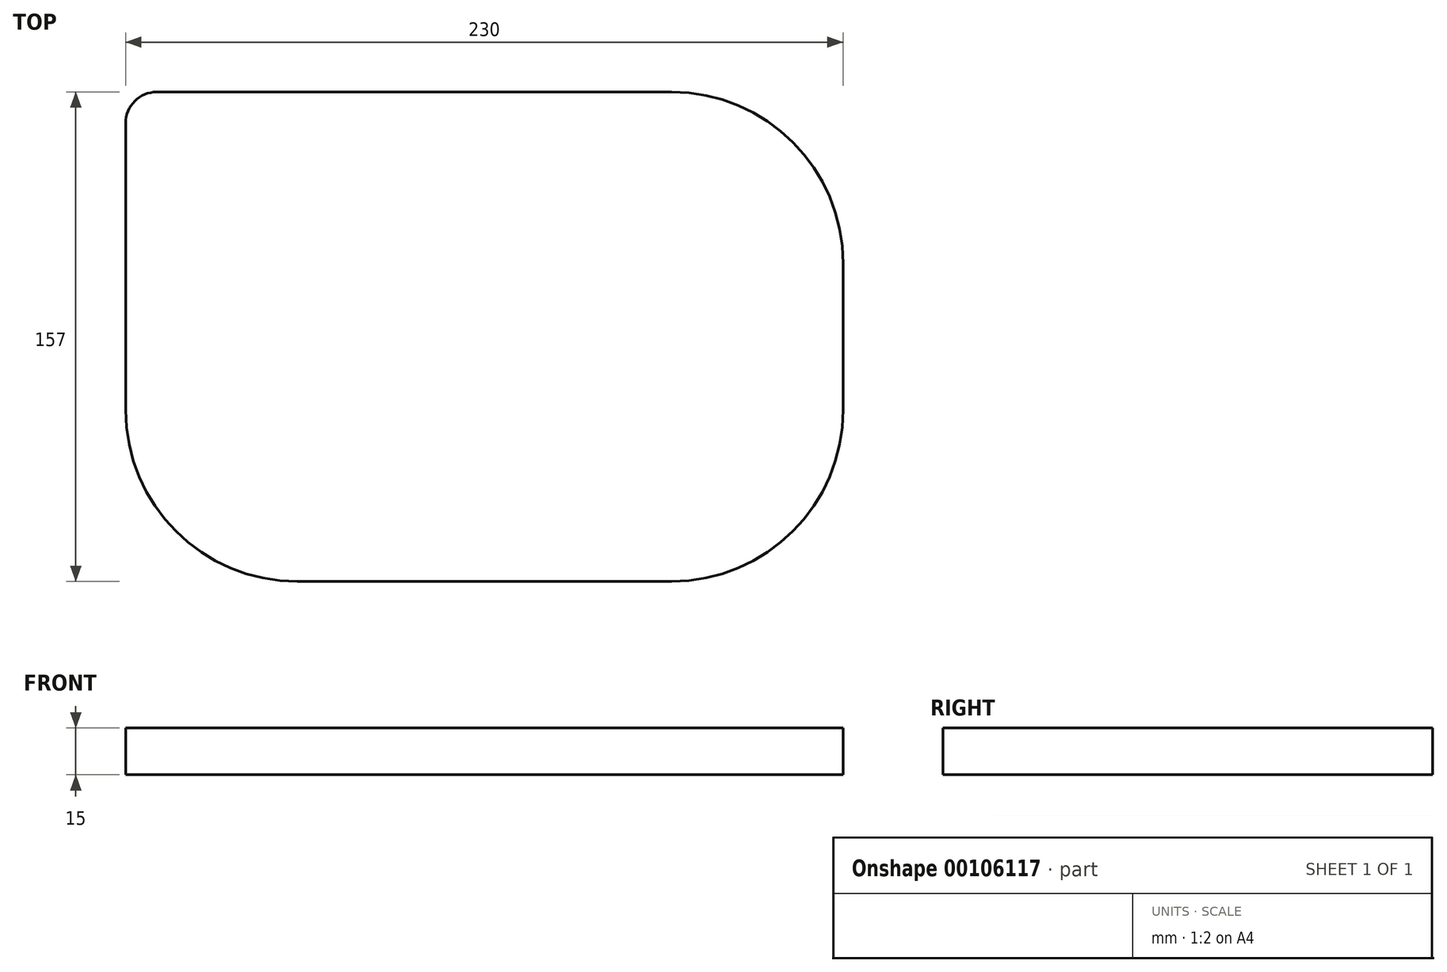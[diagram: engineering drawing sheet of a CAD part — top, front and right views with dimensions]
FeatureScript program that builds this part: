
annotation { "Feature Type Name" : "Feature", "Feature Type Description" : "" }
export const myFeature = defineFeature(function(context is Context, id is Id, definition is map)
    precondition{}
    {
        {
            var Q0;
            Q0=qCreatedBy(makeId("Top.planeOp"),FACE);
            var sketch = newSketch(context, id + "F0", { "sketchPlane" : qUnion([Q0])});
            skLineSegment(sketch, "E0.bottom", {"start": v(60, -78.5) * mm, "end": v(-60, -78.5) * mm});
            skLineSegment(sketch, "E0.top", {"start": v(60, 78.5) * mm, "end": v(-105, 78.5) * mm});
            skLineSegment(sketch, "E0.left", {"start": v(115, -23.5) * mm, "end": v(115, 23.5) * mm});
            skLineSegment(sketch, "E0.right", {"start": v(-115, -23.5) * mm, "end": v(-115, 68.5) * mm});
            skPoint(sketch, "E0.middle", {"position": v(0, 0) * mm});
            skPoint(sketch, "E1.visualSharp", {"position": v(-115, 78.5) * mm});
            skArc(sketch, "E1.filletArc", {"start": v(-105, 78.5) * mm, "mid": v(-112.07, 75.57) * mm, "end": v(-115, 68.5) * mm});
            skPoint(sketch, "E2.visualSharp", {"position": v(115, 78.5) * mm});
            skArc(sketch, "E2.filletArc", {"start": v(115, 23.5) * mm, "mid": v(98.9, 62.4) * mm, "end": v(60, 78.5) * mm});
            skPoint(sketch, "E3.visualSharp", {"position": v(115, -78.5) * mm});
            skArc(sketch, "E3.filletArc", {"start": v(60, -78.5) * mm, "mid": v(98.9, -62.4) * mm, "end": v(115, -23.5) * mm});
            skPoint(sketch, "E4.visualSharp", {"position": v(-115, -78.5) * mm});
            skArc(sketch, "E4.filletArc", {"start": v(-115, -23.5) * mm, "mid": v(-98.9, -62.4) * mm, "end": v(-60, -78.5) * mm});
            skSolve(sketch);
        }
        {
            var Q0;
            Q0 = qSketchRegion(id + "F0", true);
            extrude(context, id + "F1", {"entities" : qUnion([Q0]), "depth" : 15 * mm});
        }
    });
